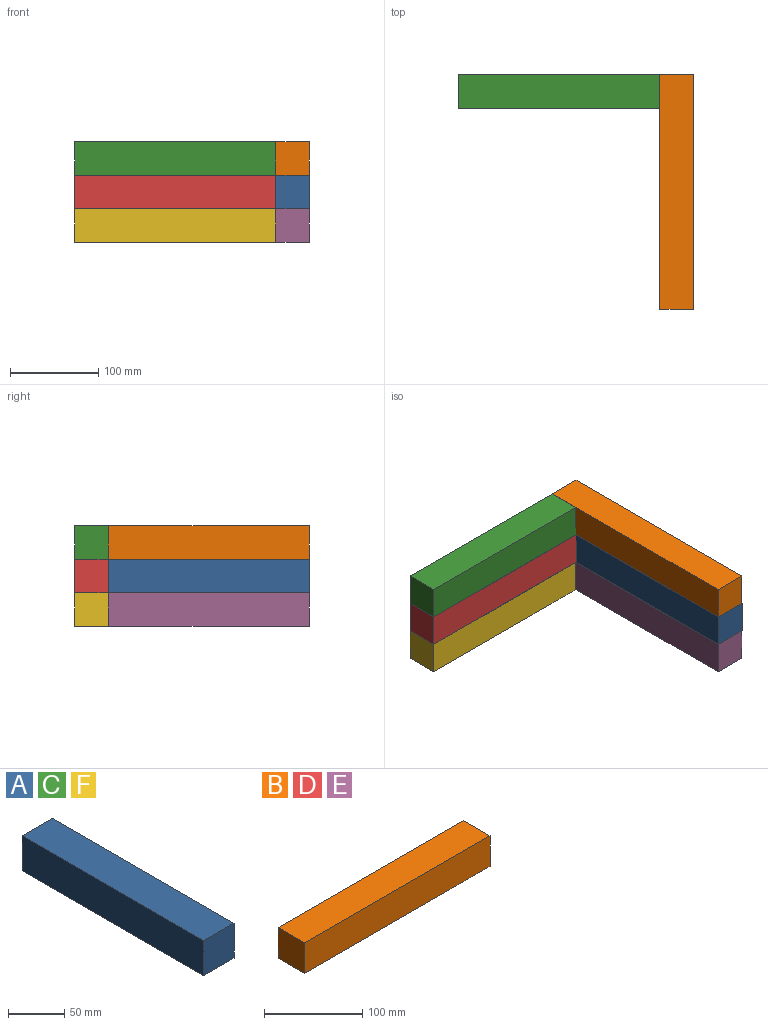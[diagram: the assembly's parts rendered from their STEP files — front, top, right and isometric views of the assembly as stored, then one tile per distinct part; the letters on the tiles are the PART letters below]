
ASSEMBLY  parts=6 mates=5
PART A: 6 faces, bbox 38.1x228.6x38.1 mm
  f0: plane 228.6x38.1mm, normal (0,0,1), area 8709.7mm2, adj f1,f3,f4,f5
  f1: plane 228.6x38.1mm, normal (1,0,0), area 8709.7mm2, adj f0,f2,f4,f5
  f2: plane 228.6x38.1mm, normal (0,0,-1), area 8709.7mm2, adj f1,f3,f4,f5
  f3: plane 228.6x38.1mm, normal (-1,0,0), area 8709.7mm2, adj f0,f2,f4,f5
  f4: plane 38.1x38.1mm, normal (0,1,0), area 1451.6mm2, adj f0,f1,f2,f3
  f5: plane 38.1x38.1mm, normal (0,-1,0), area 1451.6mm2, adj f0,f1,f2,f3
PART B: 6 faces, bbox 266.7x38.1x38.1 mm
  f0: plane 266.7x38.1mm, normal (0,-1,0), area 10161.3mm2, adj f1,f3,f4,f5
  f1: plane 38.1x38.1mm, normal (-1,0,0), area 1451.6mm2, adj f0,f2,f4,f5
  f2: plane 266.7x38.1mm, normal (0,1,0), area 10161.3mm2, adj f1,f3,f4,f5
  f3: plane 38.1x38.1mm, normal (1,0,0), area 1451.6mm2, adj f0,f2,f4,f5
  f4: plane 266.7x38.1mm, normal (0,0,-1), area 10161.3mm2, adj f0,f1,f2,f3
  f5: plane 266.7x38.1mm, normal (0,0,1), area 10161.3mm2, adj f0,f1,f2,f3
PART C: same geometry as A
PART D: same geometry as B
PART E: same geometry as B
PART F: same geometry as A
PLACE A rot(axis=(0,1,0),180deg) t=(2083.17,1364.07,45.65)mm
PLACE B rot(axis=(0.71,-0.71,0),180deg) t=(1496.2,2179.63,83.75)mm
PLACE C rot(axis=(0,0,-1),90deg) t=(1267.6,2179.63,198.05)mm fixed
PLACE D t=(718.74,1630.77,159.95)mm
PLACE E rot(axis=(0.71,-0.71,0),180deg) t=(1496.2,2179.63,7.55)mm
PLACE F rot(axis=(0,0,-1),90deg) t=(1267.6,2179.63,121.85)mm
MATE fastened B.f2 <-> C.f4  axis (-1,0,0) through (1496.2,1630.77,159.95)mm
MATE fastened E.f4 <-> D.f4  axis (0,0,1) through (1534.3,1630.77,83.75)mm
MATE fastened A.f4 <-> D.f0  axis (0,1,0) through (1534.3,1592.67,121.85)mm
MATE fastened D.f5 <-> B.f5  axis (0,0,1) through (1534.3,1630.77,121.85)mm
MATE fastened E.f2 <-> F.f4  axis (-1,0,0) through (1496.2,1630.77,45.65)mm
